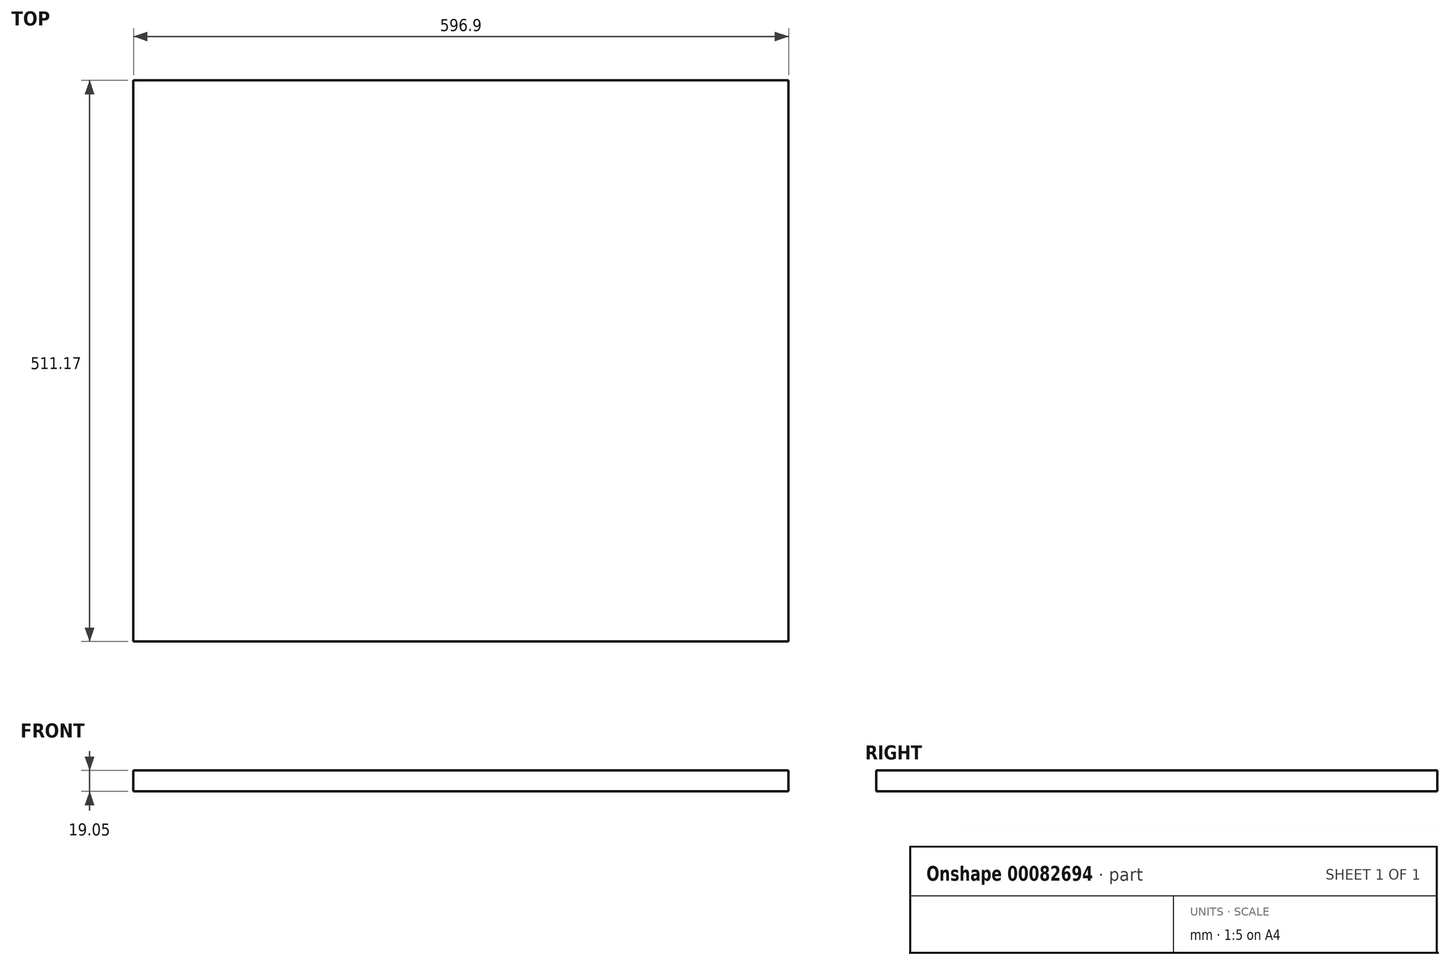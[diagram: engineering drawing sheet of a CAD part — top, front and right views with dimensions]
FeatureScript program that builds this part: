
annotation { "Feature Type Name" : "Feature", "Feature Type Description" : "" }
export const myFeature = defineFeature(function(context is Context, id is Id, definition is map)
    precondition{}
    {
        {
            var Q0;
            Q0=qCreatedBy(makeId("Top.planeOp"),FACE);
            var sketch = newSketch(context, id + "F0", { "sketchPlane" : qUnion([Q0])});
            skLineSegment(sketch, "E0.bottom", {"start": v(-249, 270.54) * mm, "end": v(347.9, 270.54) * mm});
            skLineSegment(sketch, "E0.top", {"start": v(-249, -240.63) * mm, "end": v(347.9, -240.63) * mm});
            skLineSegment(sketch, "E0.left", {"start": v(-249, 270.54) * mm, "end": v(-249, -240.63) * mm});
            skLineSegment(sketch, "E0.right", {"start": v(347.9, 270.54) * mm, "end": v(347.9, -240.63) * mm});
            skSolve(sketch);
        }
        {
            var Q0;
            Q0=qSketchRegion(id+"F0",true);
            extrude(context, id + "F1", {"entities" : qUnion([Q0]), "depth" : 19.05 * mm});
        }
    });
